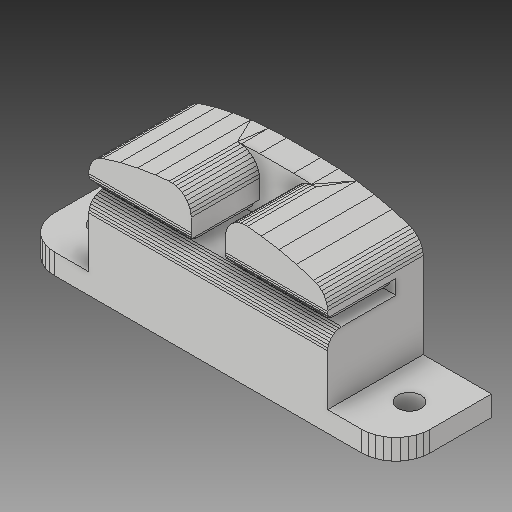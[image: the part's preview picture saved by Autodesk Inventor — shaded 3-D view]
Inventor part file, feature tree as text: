
AUTODESK INVENTOR PART (.ipt)
format: ipt  version: 2018 (Build 220112000, 112)  size: 482,816 bytes
history: native  units: mm
features: other x2, hole x1, sketch x1, projected_geometry x1
ambient origin geometry x8: Origin, YZ Plane, XZ Plane, XY Plane, X Axis, Y Axis, Z Axis, Center Point
bodies: Solid1 (feature_tree)
feature tree (5):
  other  "Y Belt Clamp"
  other  "MeshFeature1"
  hole  "Hole1"  [1 undecoded]
  sketch  "Sketch2"  dims[d0=3.4mm d1=6.0mm d2=4.0mm d3=2.0mm d4=90.0deg d5=8.0mm d6=20.594885mm]
  projected_geometry  "Projected Loop1"
note: 1 required parameter value undecoded (feature->parameter linkage not recoverable at this tier; creation-order binding heuristic only, values carry confidence <= 0.55)
